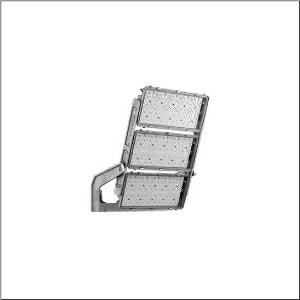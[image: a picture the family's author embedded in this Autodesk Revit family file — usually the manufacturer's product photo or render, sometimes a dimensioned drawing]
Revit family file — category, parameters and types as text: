
# Revit family: floodlight_fl_11_maxi_pro_remote___pl33t_5xa779427f01ba_72f0
name_source: partatom
category: Lighting Fixtures
units: mm (PartAtom-declared; Revit-internal decimal feet)

## family parameters
Cut with Voids When Loaded = No
Host = Face
Light Source = No
Part Type = Normal
Room Calculation Point = No
Round Connector Dimension = Use Diameter
Shared = No

## types (1)
- --- (1 x LED, 132850 lm, 953.7 W, 5000K)
    Apparent Load = 954 VA
    CIE Flux Codes = 25 74 99 100 100
    Color Rendering = 70
    Color Temperature = 5000K
    Default Elevation = 1800 mm
    Description = Floodlight FL 11  maxi  pro Remote floodlight; light control with lens of PMMA; cover panel of toughened safety glass, transparent; light distribution: PL33T, asymmetric direct distribution, LEDcolour temperature: 5000K, rated luminous flux: 132.850lm, colour rendering: CRI > 70, light colour: 750; luminous efficacy: 139lm/W; brightness control: DALI 2 (1 DALI address); with terminal, 8-pole, max. 2.5mm², mains connection: 220..240V/380..400V AC, 50/60Hz, surge voltage resistance: line to ground: 10kV, ECG replaceable separately, no afterglow with DALI off / DMX off command, LED unit replaceable without ESD environment, dustproof LED module, dimming range 10..100%; 954W floodlight with 2x LED unit of diecast aluminium, coated grey; length: 713mm / width: 651mm / height: 338mm; mounting bracket, of diecast aluminium, uncoated, natural, equipment: Longlife, protection rating (complete): IP66; insulation class (complete): insulation class I (protective earthing); certification: CE, ENEC, VDE; ball protection: ball impact resistance with accessories, impact resistance: IK07; only for outdoor installations, rated ambient temperature 10°C, permissible operating ambient temperature: -40..+30°C, permissible storage temperature: -40..+85°Cpackaging unit: 1 piece

Light Distribution: PL33T
    Height = 320 mm
    Lamp = 1 x LED
    Lamp Light Flux = 132850 lm
    Lamp Power = 953.7 W
    Lamp count = 1
    Length = 1002 mm
    Luminous efficacy = 139 lm/W
    Manufacturer = Siteco
    ModVariant = No
    Model = 5XA779427F01BA
    Mounting Place = Ceiling
    Mounting Type = Surface mounted
    Number of Poles = 1
    OnlyDefault = Yes
    Power Factor = 1
    Product Name = Floodlight FL 11 maxi pro Remote | PL33T
    Product group = floodlight | ceiling mounted
    ProductGroupID = 301
    Protection Class = Protection class I
    Protection Degree = IP 66
    RLX_Detail_Level = 1
    RLX_Emergency_Light_Flux = 0 lm
    RLX_Emergency_Type = 0
    RLX_Emergency_Type_DB = No
    RlxData = <blob elided: 52277 chars, md5=d81c3050>
    Socket = socket
    Standby Power = 0 W
    System Light Flux = 132850 lm
    System Power = 954 W
    Type Comments = factory setting: luminous flux: 100 % | dim-lin: 254 | 665 mA
    Type Image = l_1349141.jpg
    URL = http://relux.com
    VarID = @adj_096974
    Voltage = 0 V
    Weight = 0.00 kg
    Width = 655 mm

## geometry (parser evidence)
native form markers: Blend x4, Sweep x13
no freeform markers — native parametric forms only
